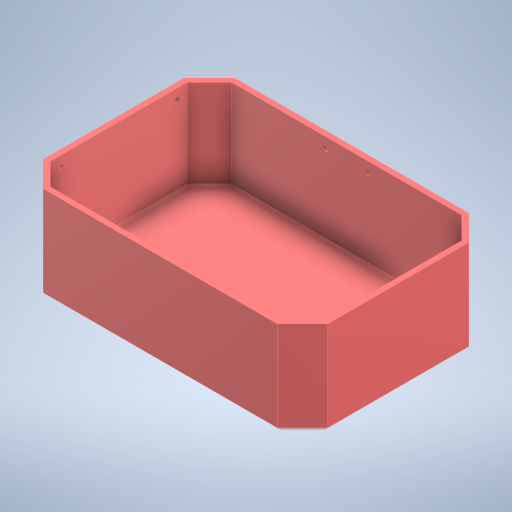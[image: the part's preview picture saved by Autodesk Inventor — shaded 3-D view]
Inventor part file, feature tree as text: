
AUTODESK INVENTOR PART (.ipt)
format: ipt  version: 2024 (Build 280153000, 153)  size: 310,784 bytes
history: native  units: in
note: dims shown in document units (in); Inventor stores cm internally (conversion verified against a paired STEP export)
features: sketch x5, extrude x4, plane x1, chamfer x1, delete_face x1, thicken_offset x1, projected_geometry x1
ambient origin geometry x8: Origin, YZ Plane, XZ Plane, XY Plane, X Axis, Y Axis, Z Axis, Center Point
bodies: Body1 (feature_tree)
feature tree (14):
  plane  "Work Plane1"
  extrude  "Extrusion3"  Depth=26.9in
  chamfer  "Chamfer1"  Distance=9.0in
  delete_face  "Delete Face3"
  thicken_offset  "Thicken3"
  sketch  "Sketch8"  dims[d20=18.1in]
  extrude  "Extrusion6"  Depth=0.5in
  extrude  "Extrusion7"  Depth=0.5in
  extrude  "Extrusion8"  Depth=0.5in
  sketch  "Sketch7"  dims[d3=8.5in d19=26.9in]
  projected_geometry  "Projected Loop3"
  sketch  "Sketch12"  dims[d21=135.0deg d22=9.0in d23=0.0in]
  sketch  "Sketch13"  dims[d24=0.5in d25=0.125in d26=45.0deg d27=0.5in]
  sketch  "Sketch14"  dims[d40=1.0in d41=1.0in d42=1.0in d43=1.0in d44=0.5in d45=0.5in d46=1.0in d47=0.0in d48=1.0in d49=0.5in d50=1.0in d51=0.0in d52=1.0in d53=2.0in d54=4.0in d55=0.5in d56=0.5in d57=1.0in d58=0.0in]
